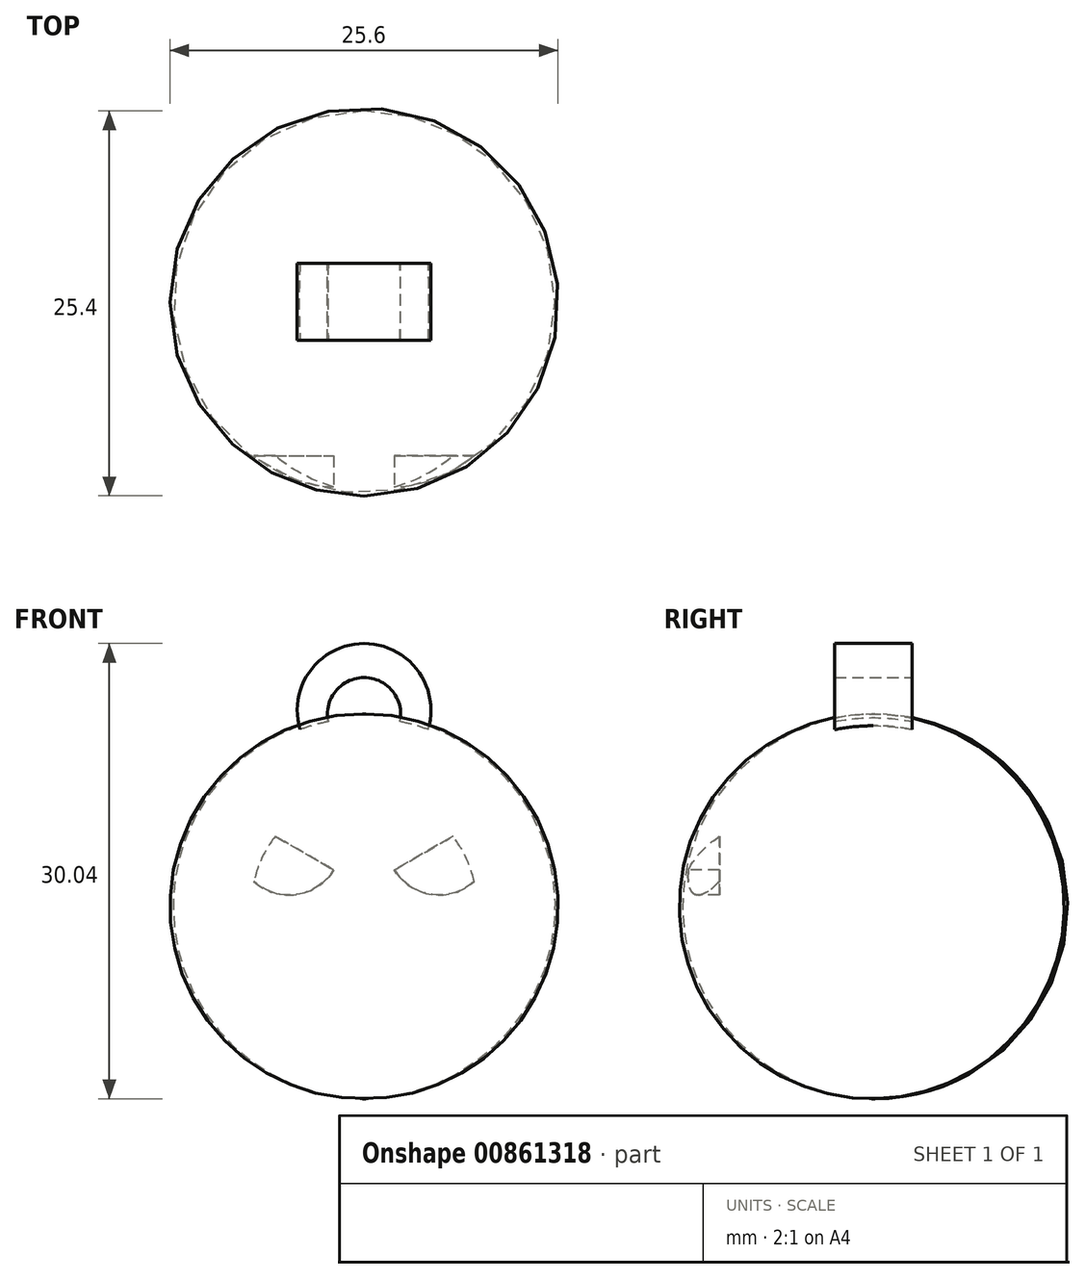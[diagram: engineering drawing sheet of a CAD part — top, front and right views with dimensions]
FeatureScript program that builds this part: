
annotation { "Feature Type Name" : "Feature", "Feature Type Description" : "" }
export const myFeature = defineFeature(function(context is Context, id is Id, definition is map)
    precondition{}
    {
        {
            var Q0;
            Q0=qCreatedBy(makeId("Front.planeOp"),FACE);
            var sketch = newSketch(context, id + "F0", { "sketchPlane" : qUnion([Q0])});
            skLineSegment(sketch, "E0", {"start": v(0, 13.06) * mm, "end": v(0, -12.34) * mm});
            skArc(sketch, "E1", {"start": v(0, -12.34) * mm, "mid": v(12.6, 0.36) * mm, "end": v(0, 13.06) * mm});
            skSolve(sketch);
        }
        {
            var Q0;
            Q0=makeQuery(id+"F0.imprint","IMPRINT",FACE,{"disambiguationData":[TD([[makeQuery(id+"F0.imprint","IMPRINT",EDGE,{"derivedFrom":sQuery(id+"F0.wireOp",EDGE,"E0")}),1.0]])]});
            var Q1;
            Q1=sQuery(id+"F0.wireOp",EDGE,"E0");
            revolve(context, id + "F1", {"surfaceOperationType" : NewSurfaceOperationType.NEW, "entities" : qUnion([Q0]), "axis" : qUnion([Q1]), "revolveType" : RevolveType.FULL});
        }
        {
            var Q0;
            Q0=qCreatedBy(makeId("Front.planeOp"),FACE);
            cPlane(context, id + "F2", {"entities" : qUnion([Q0]), "cplaneType" : CPlaneType.OFFSET, "offset" : 15.24 * mm, "width" : 152.4 * mm, "height" : 152.4 * mm});
        }
        {
            var Q0;
            Q0=qCreatedBy(id+"F2.planeOp",FACE);
            var sketch = newSketch(context, id + "F3", { "sketchPlane" : qUnion([Q0])});
            skLineSegment(sketch, "E2", {"start": v(-7.96, 6.2) * mm, "end": v(-2, 2.76) * mm});
            skArc(sketch, "E3", {"start": v(-7.96, 6.2) * mm, "mid": v(-6.66, 1.56) * mm, "end": v(-2, 2.76) * mm});
            skLineSegment(sketch, "E4.MirrorCS", {"start": v(7.96, 6.2) * mm, "end": v(2, 2.76) * mm});
            skArc(sketch, "E5.MirrorCS", {"start": v(7.96, 6.2) * mm, "mid": v(6.66, 1.56) * mm, "end": v(2, 2.76) * mm});
            skSolve(sketch);
        }
        {
            var Q0;
            Q0=makeQuery(id+"F3.imprint","IMPRINT",FACE,{"disambiguationData":[TD([[makeQuery(id+"F3.imprint","IMPRINT",EDGE,{"derivedFrom":sQuery(id+"F3.wireOp",EDGE,"E2")}),-1.0]])]});
            var Q1;
            Q1=makeQuery(id+"F3.imprint","IMPRINT",FACE,{"disambiguationData":[TD([[makeQuery(id+"F3.imprint","IMPRINT",EDGE,{"derivedFrom":sQuery(id+"F3.wireOp",EDGE,"E4.MirrorCS")}),1.0]])]});
            extrude(context, id + "F4", {"entities" : qUnion([Q0, Q1]), "operationType" : NewBodyOperationType.REMOVE, "oppositeDirection" : true, "depth" : 5.08 * mm, "offsetDistance" : 25.4 * mm});
        }
        {
            var Q0;
            Q0=qCreatedBy(makeId("Front.planeOp"),FACE);
            var sketch = newSketch(context, id + "F5", { "sketchPlane" : qUnion([Q0])});
            skLineSegment(sketch, "E6", {"start": v(0, 11.8) * mm, "end": v(0, 17.7) * mm});
            skLineSegment(sketch, "E7", {"start": v(0, 11.8) * mm, "end": v(-4.15, 11.8) * mm});
            skLineSegment(sketch, "E8.MirrorCS", {"start": v(0, 11.8) * mm, "end": v(4.15, 11.8) * mm});
            skArc(sketch, "E9", {"start": v(4.15, 11.8) * mm, "mid": v(0, 17.7) * mm, "end": v(-4.15, 11.8) * mm});
            skArc(sketch, "E10", {"start": v(2.07, 11.8) * mm, "mid": v(0, 15.45) * mm, "end": v(-2.07, 11.8) * mm});
            skSolve(sketch);
        }
        {
            var Q0;
            {var subQ0=sQuery(id+"F5.wireOp",EDGE,"E9");var subQ1=sQuery(id+"F5.wireOp",EDGE,"E6");var subQ2=makeQuery(id+"F5.imprint","INTERSECT",VERTEX,{"derivedFrom":[subQ1,subQ0]});Q0=makeQuery(id+"F5.imprint","IMPRINT",FACE,{"disambiguationData":[TD([[makeQuery(id+"F5.imprint","IMPRINT",EDGE,{"disambiguationData":[TD([[subQ2,1.0]])],"derivedFrom":subQ1}),1.0]])]});}
            var Q1;
            {var subQ0=sQuery(id+"F5.wireOp",EDGE,"E9");var subQ1=sQuery(id+"F5.wireOp",EDGE,"E6");var subQ2=makeQuery(id+"F5.imprint","INTERSECT",VERTEX,{"derivedFrom":[subQ1,subQ0]});Q1=makeQuery(id+"F5.imprint","IMPRINT",FACE,{"disambiguationData":[TD([[makeQuery(id+"F5.imprint","IMPRINT",EDGE,{"disambiguationData":[TD([[subQ2,1.0]])],"derivedFrom":subQ1}),-1.0]])]});}
            extrude(context, id + "F6", {"entities" : qUnion([Q0, Q1]), "operationType" : NewBodyOperationType.ADD, "endBound" : BoundingType.SYMMETRIC, "depth" : 5.08 * mm, "offsetDistance" : 25.4 * mm});
        }
    });
